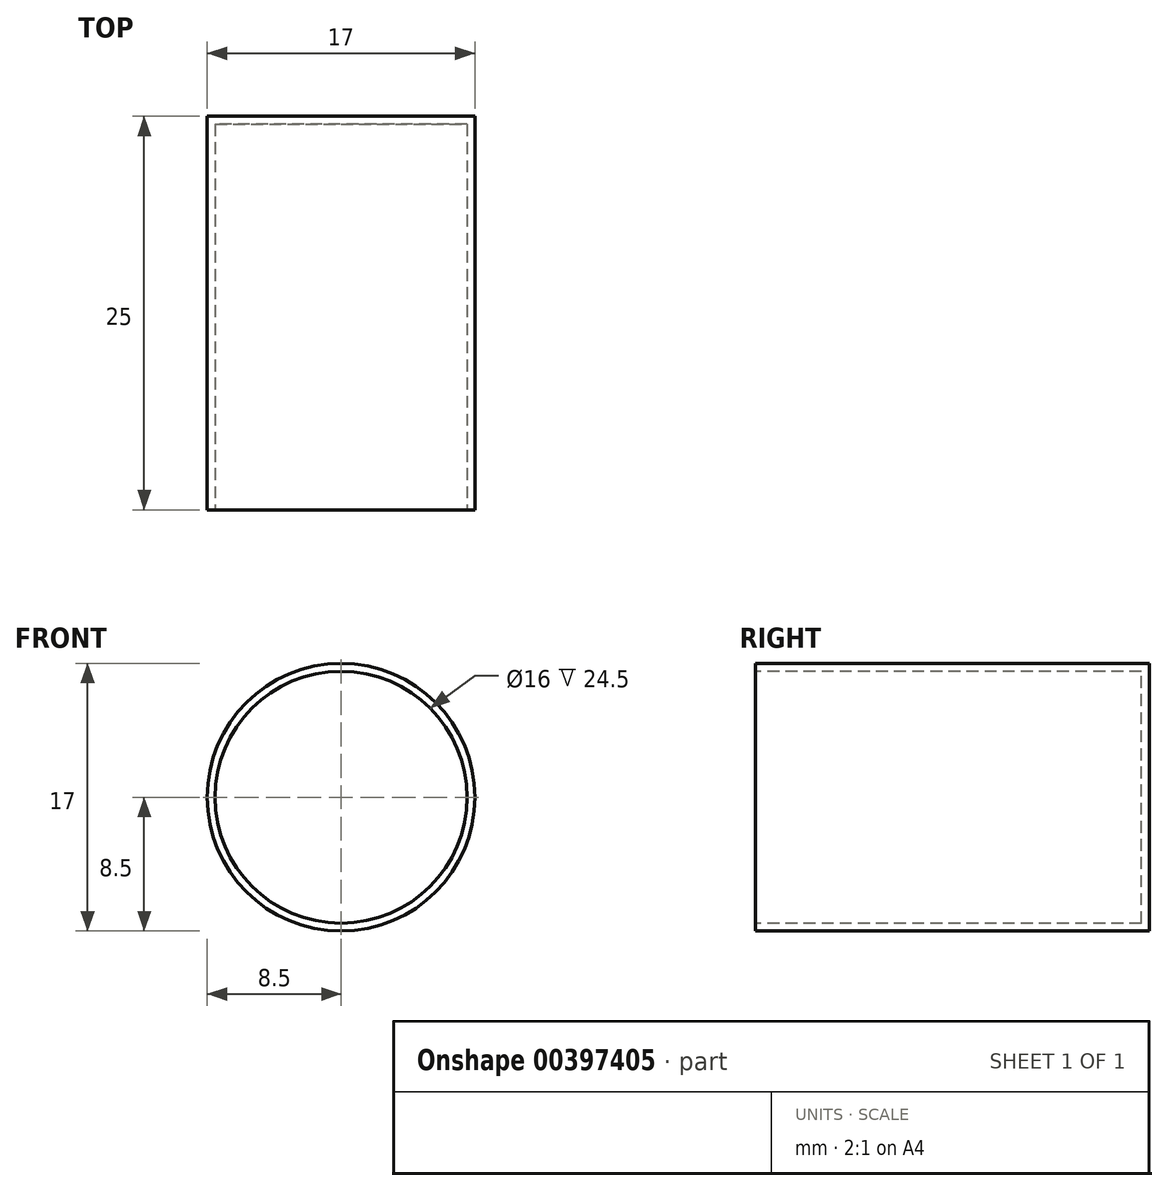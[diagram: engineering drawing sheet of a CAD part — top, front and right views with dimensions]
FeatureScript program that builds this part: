
annotation { "Feature Type Name" : "Feature", "Feature Type Description" : "" }
export const myFeature = defineFeature(function(context is Context, id is Id, definition is map)
    precondition{}
    {
        {
            var Q0;
            Q0=qCreatedBy(makeId("Front.planeOp"),FACE);
            var sketch = newSketch(context, id + "F0", { "sketchPlane" : qUnion([Q0])});
            skCircle(sketch, "E0", {"center": v(0, 0) * mm, "radius": 8.5 * mm});
            skSolve(sketch);
        }
        {
            var Q0;
            Q0 = qSketchRegion(id + "F0", true);
            extrude(context, id + "F1", {"entities" : qUnion([Q0]), "oppositeDirection" : true, "depth" : 25 * mm});
        }
        {
            var Q0;
            Q0=makeQuery(id+"F1.opExtrude","CAP_FACE",FACE,{"disambiguationData":[OSD([sQuery(id+"F0.wireOp",EDGE,"E0")])],"isStart":true});
            shell(context, id + "F2", {"entities" : qUnion([Q0]), "thickness" : .5 * mm});
        }
    });
